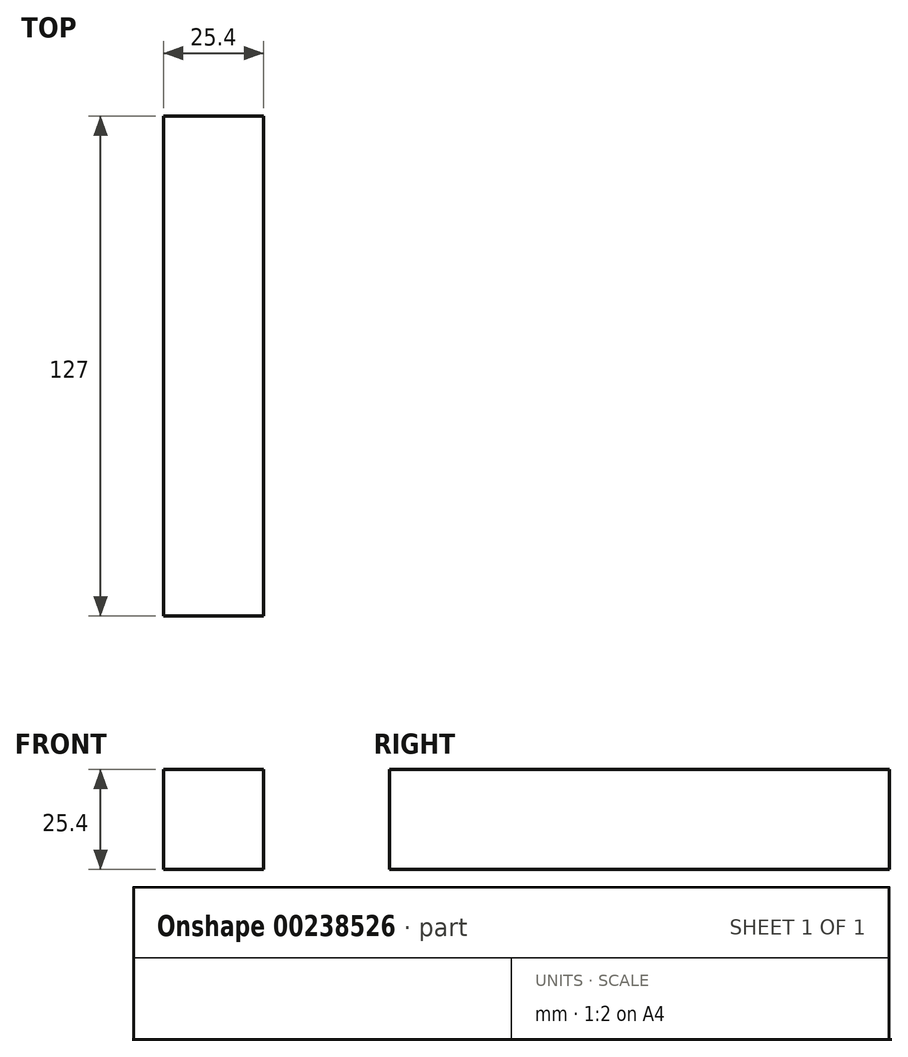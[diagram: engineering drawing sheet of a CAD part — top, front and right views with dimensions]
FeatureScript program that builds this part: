
annotation { "Feature Type Name" : "Feature", "Feature Type Description" : "" }
export const myFeature = defineFeature(function(context is Context, id is Id, definition is map)
    precondition{}
    {
        {
            var Q0;
            Q0=qCreatedBy(makeId("Front.planeOp"),FACE);
            var sketch = newSketch(context, id + "F0", { "sketchPlane" : qUnion([Q0])});
            skLineSegment(sketch, "E0.bottom", {"start": v(-139.7, 13.28) * mm, "end": v(-114.3, 13.28) * mm});
            skLineSegment(sketch, "E0.top", {"start": v(-139.7, -12.12) * mm, "end": v(-114.3, -12.12) * mm});
            skLineSegment(sketch, "E0.left", {"start": v(-139.7, 13.28) * mm, "end": v(-139.7, -12.12) * mm});
            skLineSegment(sketch, "E0.right", {"start": v(-114.3, 13.28) * mm, "end": v(-114.3, -12.12) * mm});
            skLineSegment(sketch, "E1", {"start": v(-139.7, 13.28) * mm, "end": v(-114.3, -12.12) * mm, "construction": true});
            skLineSegment(sketch, "E2", {"start": v(-114.3, 13.28) * mm, "end": v(-139.7, -12.12) * mm, "construction": true});
            skPoint(sketch, "E3", {"position": v(-127, 0.58) * mm});
            skLineSegment(sketch, "E4", {"start": v(-63.54, 15.63) * mm, "end": v(-85.08, 15.63) * mm});
            skLineSegment(sketch, "E5", {"start": v(-85.08, 15.63) * mm, "end": v(-85.08, -2.98) * mm});
            skLineSegment(sketch, "E6", {"start": v(-85.08, -2.98) * mm, "end": v(-63.54, -2.98) * mm});
            skLineSegment(sketch, "E7", {"start": v(-63.54, -2.98) * mm, "end": v(-63.54, 15.63) * mm});
            skLineSegment(sketch, "E8", {"start": v(-63.54, 15.63) * mm, "end": v(-63.54, 15.63) * mm});
            skSolve(sketch);
        }
        {
            var Q0;
            Q0=makeQuery(id+"F0.imprint","IMPRINT",FACE,{"disambiguationData":[TD([[makeQuery(id+"F0.imprint","IMPRINT",EDGE,{"derivedFrom":sQuery(id+"F0.wireOp",EDGE,"E0.bottom")}),-1.0]])]});
            extrude(context, id + "F1", {"entities" : qUnion([Q0]), "depth" : 127 * mm});
        }
    });
